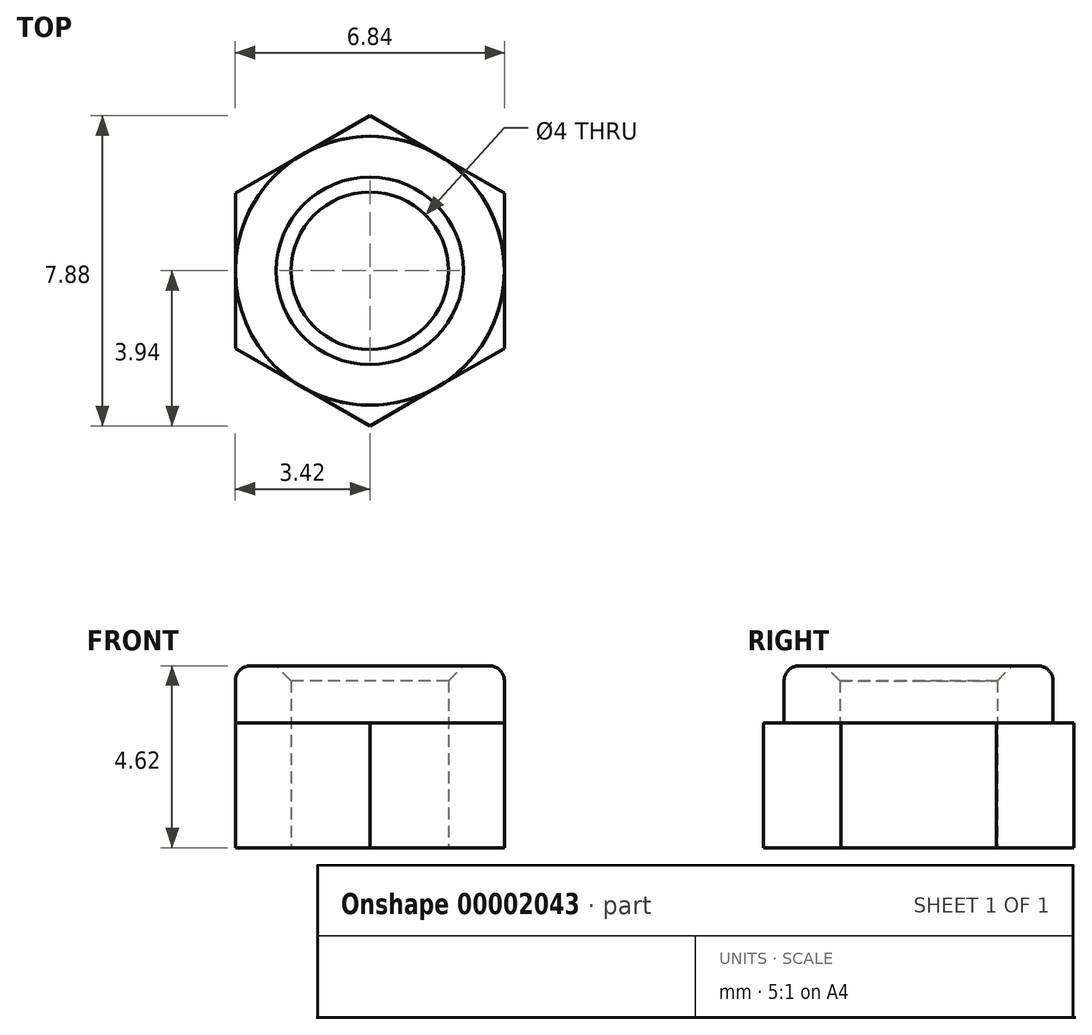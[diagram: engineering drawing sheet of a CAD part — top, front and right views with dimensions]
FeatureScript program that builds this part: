
annotation { "Feature Type Name" : "Feature", "Feature Type Description" : "" }
export const myFeature = defineFeature(function(context is Context, id is Id, definition is map)
    precondition{}
    {
        {
            var Q0;
            Q0=qCreatedBy(makeId("Top.planeOp"),FACE);
            var sketch = newSketch(context, id + "F0", { "sketchPlane" : qUnion([Q0])});
            skCircle(sketch, "E0.cCircle", {"center": v(0, 0) * mm, "radius": 3.42 * mm, "construction": true});
            skLineSegment(sketch, "E0.0", {"start": v(3.42, 1.97) * mm, "end": v(3.42, -1.97) * mm});
            skLineSegment(sketch, "E0.1", {"start": v(3.42, -1.97) * mm, "end": v(0, -3.94) * mm});
            skLineSegment(sketch, "E0.2", {"start": v(0, -3.94) * mm, "end": v(-3.42, -1.97) * mm});
            skLineSegment(sketch, "E0.3", {"start": v(-3.42, -1.97) * mm, "end": v(-3.42, 1.97) * mm});
            skLineSegment(sketch, "E0.4", {"start": v(-3.42, 1.97) * mm, "end": v(0, 3.94) * mm});
            skLineSegment(sketch, "E0.5", {"start": v(0, 3.94) * mm, "end": v(3.42, 1.97) * mm});
            skPoint(sketch, "E0.0.midPoint", {"position": v(3.42, 0) * mm});
            skCircle(sketch, "E1", {"center": v(0, 0) * mm, "radius": 2 * mm});
            skSolve(sketch);
        }
        {
            var Q0;
            Q0 = qSketchRegion(id + "F0", true);
            extrude(context, id + "F1", {"entities" : qUnion([Q0]), "depth" : 3.17 * mm});
        }
        {
            var Q0;
            Q0=makeQuery(id+"F1.opExtrude","CAP_FACE",FACE,{"disambiguationData":[OSD([sQuery(id+"F0.wireOp",EDGE,"E0.0"),sQuery(id+"F0.wireOp",EDGE,"E0.1"),sQuery(id+"F0.wireOp",EDGE,"E0.2"),sQuery(id+"F0.wireOp",EDGE,"E0.3"),sQuery(id+"F0.wireOp",EDGE,"E0.4"),sQuery(id+"F0.wireOp",EDGE,"E0.5"),sQuery(id+"F0.wireOp",EDGE,"E1")])],"isStart":false});
            var sketch = newSketch(context, id + "F2", { "sketchPlane" : qUnion([Q0])});
            skCircle(sketch, "E2", {"center": v(0, 0) * mm, "radius": 3.42 * mm});
            skCircle(sketch, "E3", {"center": v(0, 0) * mm, "radius": 2 * mm});
            skSolve(sketch);
        }
        {
            var Q0;
            Q0 = qSketchRegion(id + "F2", true);
            extrude(context, id + "F3", {"entities" : qUnion([Q0]), "operationType" : NewBodyOperationType.ADD, "depth" : 1.45 * mm});
        }
        {
            var Q0;
            Q0=makeQuery(id+"F3.opExtrude","CAP_EDGE",EDGE,{"disambiguationData":[OSD([sQuery(id+"F2.wireOp",EDGE,"E2")])],"isStart":false});
            fillet(context, id + "F4", {"entities" : qUnion([Q0]), "radius" : 0.38 * mm, "tangentPropagation" : true, "allowEdgeOverflow" : false});
        }
        {
            var Q0;
            Q0=makeQuery(id+"F3.opExtrude","CAP_EDGE",EDGE,{"disambiguationData":[OSD([sQuery(id+"F2.wireOp",EDGE,"E3")])],"isStart":false});
            chamfer(context, id + "F5", {"entities" : qUnion([Q0]), "width" : 0.38 * mm, "tangentPropagation" : true});
        }
    });
